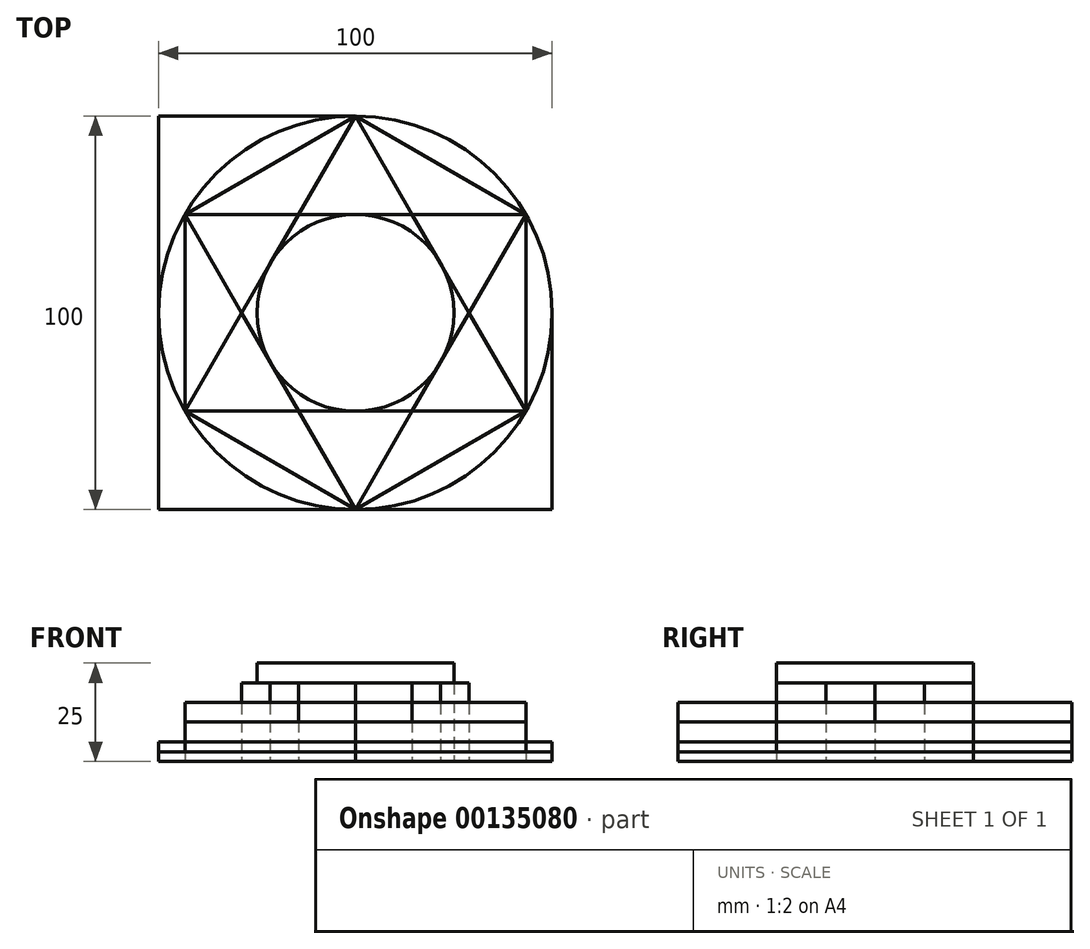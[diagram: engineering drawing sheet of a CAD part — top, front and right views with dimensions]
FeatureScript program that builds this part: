
annotation { "Feature Type Name" : "Feature", "Feature Type Description" : "" }
export const myFeature = defineFeature(function(context is Context, id is Id, definition is map)
    precondition{}
    {
        {
            var Q0;
            Q0=qCreatedBy(makeId("Top.planeOp"),FACE);
            var sketch = newSketch(context, id + "F0", { "sketchPlane" : qUnion([Q0])});
            skCircle(sketch, "E0", {"center": v(0, 0) * mm, "radius": 50 * mm});
            skCircle(sketch, "E1.cCircle", {"center": v(0, 0) * mm, "radius": 50 * mm, "construction": true});
            skLineSegment(sketch, "E1.0", {"start": v(0, 50) * mm, "end": v(43.3, 25) * mm});
            skLineSegment(sketch, "E1.1", {"start": v(43.3, 25) * mm, "end": v(43.3, -25) * mm});
            skLineSegment(sketch, "E1.2", {"start": v(43.3, -25) * mm, "end": v(0, -50) * mm});
            skLineSegment(sketch, "E1.3", {"start": v(0, -50) * mm, "end": v(-43.3, -25) * mm});
            skLineSegment(sketch, "E1.4", {"start": v(-43.3, -25) * mm, "end": v(-43.3, 25) * mm});
            skLineSegment(sketch, "E1.5", {"start": v(-43.3, 25) * mm, "end": v(0, 50) * mm});
            skLineSegment(sketch, "E2", {"start": v(0, 50) * mm, "end": v(-43.3, -25) * mm});
            skLineSegment(sketch, "E3", {"start": v(-43.3, -25) * mm, "end": v(43.3, -25) * mm});
            skLineSegment(sketch, "E4", {"start": v(43.3, -25) * mm, "end": v(0, 50) * mm});
            skLineSegment(sketch, "E5", {"start": v(-43.3, 25) * mm, "end": v(43.3, 25) * mm});
            skLineSegment(sketch, "E6", {"start": v(43.3, 25) * mm, "end": v(0, -50) * mm});
            skLineSegment(sketch, "E7", {"start": v(0, -50) * mm, "end": v(-43.3, 25) * mm});
            skCircle(sketch, "E8", {"center": v(0, 0) * mm, "radius": 25 * mm});
            skLineSegment(sketch, "E9", {"start": v(50, 50) * mm, "end": v(50, 0) * mm});
            skLineSegment(sketch, "E10.0", {"start": v(-50, 50) * mm, "end": v(50, 50) * mm});
            skLineSegment(sketch, "E10.1", {"start": v(50, 50) * mm, "end": v(50, -50) * mm});
            skLineSegment(sketch, "E10.2", {"start": v(50, -50) * mm, "end": v(-50, -50) * mm});
            skLineSegment(sketch, "E10.3", {"start": v(-50, -50) * mm, "end": v(-50, 50) * mm});
            skPoint(sketch, "E10.0.midPoint", {"position": v(0, 50) * mm});
            skSolve(sketch);
        }
        {
            var Q0;
            {var subQ0=sQuery(id+"F0.wireOp",EDGE,"E8");var subQ5=makeQuery(id+"F0.imprint","INTERSECT",VERTEX,{"derivedFrom":[sQuery(id+"F0.wireOp",EDGE,"E4"),subQ0]});Q0=makeQuery(id+"F0.imprint","IMPRINT",FACE,{"disambiguationData":[TD([[makeQuery(id+"F0.imprint","IMPRINT",EDGE,{"disambiguationData":[TD([[subQ5,-1.0]])],"derivedFrom":subQ0}),1.0]])]});}
            extrude(context, id + "F1", {"entities" : qUnion([Q0]), "depth" : 25 * mm});
        }
        {
            var Q0;
            {var subQ0=sQuery(id+"F0.wireOp",EDGE,"E5");var subQ1=sQuery(id+"F0.wireOp",EDGE,"E2");var subQ2=makeQuery(id+"F0.imprint","INTERSECT",VERTEX,{"derivedFrom":[subQ1,subQ0]});Q0=makeQuery(id+"F0.imprint","IMPRINT",FACE,{"disambiguationData":[TD([[makeQuery(id+"F0.imprint","IMPRINT",EDGE,{"disambiguationData":[TD([[subQ2,-1.0]])],"derivedFrom":subQ1}),1.0]])]});}
            var Q1;
            {var subQ0=sQuery(id+"F0.wireOp",EDGE,"E6");var subQ1=sQuery(id+"F0.wireOp",EDGE,"E4");var subQ2=makeQuery(id+"F0.imprint","INTERSECT",VERTEX,{"derivedFrom":[subQ1,subQ0]});Q1=makeQuery(id+"F0.imprint","IMPRINT",FACE,{"disambiguationData":[TD([[makeQuery(id+"F0.imprint","IMPRINT",EDGE,{"disambiguationData":[TD([[subQ2,-1.0]])],"derivedFrom":subQ1}),1.0]])]});}
            var Q2;
            {var subQ0=sQuery(id+"F0.wireOp",EDGE,"E8");var subQ1=sQuery(id+"F0.wireOp",EDGE,"E4");var subQ2=makeQuery(id+"F0.imprint","INTERSECT",VERTEX,{"derivedFrom":[subQ1,subQ0]});Q2=makeQuery(id+"F0.imprint","IMPRINT",FACE,{"disambiguationData":[TD([[makeQuery(id+"F0.imprint","IMPRINT",EDGE,{"disambiguationData":[TD([[subQ2,-1.0]])],"derivedFrom":subQ1}),1.0]])]});}
            var Q3;
            {var subQ0=sQuery(id+"F0.wireOp",EDGE,"E8");var subQ1=sQuery(id+"F0.wireOp",EDGE,"E3");var subQ2=makeQuery(id+"F0.imprint","INTERSECT",VERTEX,{"derivedFrom":[subQ1,subQ0]});Q3=makeQuery(id+"F0.imprint","IMPRINT",FACE,{"disambiguationData":[TD([[makeQuery(id+"F0.imprint","IMPRINT",EDGE,{"disambiguationData":[TD([[subQ2,-1.0]])],"derivedFrom":subQ1}),1.0]])]});}
            var Q4;
            {var subQ0=sQuery(id+"F0.wireOp",EDGE,"E7");var subQ1=sQuery(id+"F0.wireOp",EDGE,"E3");var subQ2=makeQuery(id+"F0.imprint","INTERSECT",VERTEX,{"derivedFrom":[subQ1,subQ0]});Q4=makeQuery(id+"F0.imprint","IMPRINT",FACE,{"disambiguationData":[TD([[makeQuery(id+"F0.imprint","IMPRINT",EDGE,{"disambiguationData":[TD([[subQ2,-1.0]])],"derivedFrom":subQ1}),1.0]])]});}
            var Q5;
            {var subQ0=sQuery(id+"F0.wireOp",EDGE,"E8");var subQ1=sQuery(id+"F0.wireOp",EDGE,"E2");var subQ2=makeQuery(id+"F0.imprint","INTERSECT",VERTEX,{"derivedFrom":[subQ1,subQ0]});Q5=makeQuery(id+"F0.imprint","IMPRINT",FACE,{"disambiguationData":[TD([[makeQuery(id+"F0.imprint","IMPRINT",EDGE,{"disambiguationData":[TD([[subQ2,-1.0]])],"derivedFrom":subQ1}),1.0]])]});}
            extrude(context, id + "F2", {"entities" : qUnion([Q0, Q1, Q2, Q3, Q4, Q5]), "depth" : 20 * mm});
        }
        {
            var Q0;
            {var subQ1=sQuery(id+"F0.wireOp",EDGE,"E2");var subQ3=sQuery(id+"F0.wireOp",EDGE,"E5");var subQ4=makeQuery(id+"F0.imprint","INTERSECT",VERTEX,{"derivedFrom":[subQ1,subQ3]});Q0=makeQuery(id+"F0.imprint","IMPRINT",FACE,{"disambiguationData":[TD([[makeQuery(id+"F0.imprint","IMPRINT",EDGE,{"disambiguationData":[TD([[subQ4,-1.0]])],"derivedFrom":subQ3}),1.0]])]});}
            var Q1;
            {var subQ0=sQuery(id+"F0.wireOp",EDGE,"E6");var subQ1=sQuery(id+"F0.wireOp",EDGE,"E4");var subQ2=makeQuery(id+"F0.imprint","INTERSECT",VERTEX,{"derivedFrom":[subQ1,subQ0]});Q1=makeQuery(id+"F0.imprint","IMPRINT",FACE,{"disambiguationData":[TD([[makeQuery(id+"F0.imprint","IMPRINT",EDGE,{"disambiguationData":[TD([[subQ2,-1.0]])],"derivedFrom":subQ1}),-1.0]])]});}
            var Q2;
            {var subQ0=sQuery(id+"F0.wireOp",EDGE,"E4");var subQ3=sQuery(id+"F0.wireOp",EDGE,"E6");var subQ5=makeQuery(id+"F0.imprint","INTERSECT",VERTEX,{"derivedFrom":[subQ0,subQ3]});Q2=makeQuery(id+"F0.imprint","IMPRINT",FACE,{"disambiguationData":[TD([[makeQuery(id+"F0.imprint","IMPRINT",EDGE,{"disambiguationData":[TD([[subQ5,-1.0]])],"derivedFrom":subQ3}),1.0]])]});}
            var Q3;
            {var subQ0=sQuery(id+"F0.wireOp",EDGE,"E7");var subQ1=sQuery(id+"F0.wireOp",EDGE,"E3");var subQ2=makeQuery(id+"F0.imprint","INTERSECT",VERTEX,{"derivedFrom":[subQ1,subQ0]});Q3=makeQuery(id+"F0.imprint","IMPRINT",FACE,{"disambiguationData":[TD([[makeQuery(id+"F0.imprint","IMPRINT",EDGE,{"disambiguationData":[TD([[subQ2,-1.0]])],"derivedFrom":subQ1}),-1.0]])]});}
            var Q4;
            {var subQ0=sQuery(id+"F0.wireOp",EDGE,"E3");var subQ3=sQuery(id+"F0.wireOp",EDGE,"E7");var subQ5=makeQuery(id+"F0.imprint","INTERSECT",VERTEX,{"derivedFrom":[subQ0,subQ3]});Q4=makeQuery(id+"F0.imprint","IMPRINT",FACE,{"disambiguationData":[TD([[makeQuery(id+"F0.imprint","IMPRINT",EDGE,{"disambiguationData":[TD([[subQ5,-1.0]])],"derivedFrom":subQ3}),1.0]])]});}
            var Q5;
            {var subQ0=sQuery(id+"F0.wireOp",EDGE,"E5");var subQ1=sQuery(id+"F0.wireOp",EDGE,"E2");var subQ2=makeQuery(id+"F0.imprint","INTERSECT",VERTEX,{"derivedFrom":[subQ1,subQ0]});Q5=makeQuery(id+"F0.imprint","IMPRINT",FACE,{"disambiguationData":[TD([[makeQuery(id+"F0.imprint","IMPRINT",EDGE,{"disambiguationData":[TD([[subQ2,-1.0]])],"derivedFrom":subQ1}),-1.0]])]});}
            var Q6;
            {var subQ0=sQuery(id+"F0.wireOp",EDGE,"E5");var subQ1=sQuery(id+"F0.wireOp",EDGE,"E2");var subQ2=makeQuery(id+"F0.imprint","INTERSECT",VERTEX,{"derivedFrom":[subQ1,subQ0]});Q6=makeQuery(id+"F0.imprint","IMPRINT",FACE,{"disambiguationData":[TD([[makeQuery(id+"F0.imprint","IMPRINT",EDGE,{"disambiguationData":[TD([[subQ2,-1.0]])],"derivedFrom":subQ1}),1.0]])]});}
            var Q7;
            {var subQ0=sQuery(id+"F0.wireOp",EDGE,"E8");var subQ1=sQuery(id+"F0.wireOp",EDGE,"E4");var subQ2=makeQuery(id+"F0.imprint","INTERSECT",VERTEX,{"derivedFrom":[subQ1,subQ0]});Q7=makeQuery(id+"F0.imprint","IMPRINT",FACE,{"disambiguationData":[TD([[makeQuery(id+"F0.imprint","IMPRINT",EDGE,{"disambiguationData":[TD([[subQ2,-1.0]])],"derivedFrom":subQ1}),1.0]])]});}
            var Q8;
            {var subQ0=sQuery(id+"F0.wireOp",EDGE,"E6");var subQ1=sQuery(id+"F0.wireOp",EDGE,"E4");var subQ2=makeQuery(id+"F0.imprint","INTERSECT",VERTEX,{"derivedFrom":[subQ1,subQ0]});Q8=makeQuery(id+"F0.imprint","IMPRINT",FACE,{"disambiguationData":[TD([[makeQuery(id+"F0.imprint","IMPRINT",EDGE,{"disambiguationData":[TD([[subQ2,-1.0]])],"derivedFrom":subQ1}),1.0]])]});}
            var Q9;
            {var subQ0=sQuery(id+"F0.wireOp",EDGE,"E8");var subQ1=sQuery(id+"F0.wireOp",EDGE,"E3");var subQ2=makeQuery(id+"F0.imprint","INTERSECT",VERTEX,{"derivedFrom":[subQ1,subQ0]});Q9=makeQuery(id+"F0.imprint","IMPRINT",FACE,{"disambiguationData":[TD([[makeQuery(id+"F0.imprint","IMPRINT",EDGE,{"disambiguationData":[TD([[subQ2,-1.0]])],"derivedFrom":subQ1}),1.0]])]});}
            var Q10;
            {var subQ0=sQuery(id+"F0.wireOp",EDGE,"E7");var subQ1=sQuery(id+"F0.wireOp",EDGE,"E3");var subQ2=makeQuery(id+"F0.imprint","INTERSECT",VERTEX,{"derivedFrom":[subQ1,subQ0]});Q10=makeQuery(id+"F0.imprint","IMPRINT",FACE,{"disambiguationData":[TD([[makeQuery(id+"F0.imprint","IMPRINT",EDGE,{"disambiguationData":[TD([[subQ2,-1.0]])],"derivedFrom":subQ1}),1.0]])]});}
            var Q11;
            {var subQ0=sQuery(id+"F0.wireOp",EDGE,"E8");var subQ1=sQuery(id+"F0.wireOp",EDGE,"E2");var subQ2=makeQuery(id+"F0.imprint","INTERSECT",VERTEX,{"derivedFrom":[subQ1,subQ0]});Q11=makeQuery(id+"F0.imprint","IMPRINT",FACE,{"disambiguationData":[TD([[makeQuery(id+"F0.imprint","IMPRINT",EDGE,{"disambiguationData":[TD([[subQ2,-1.0]])],"derivedFrom":subQ1}),1.0]])]});}
            var Q12;
            {var subQ0=sQuery(id+"F0.wireOp",EDGE,"E8");var subQ5=makeQuery(id+"F0.imprint","INTERSECT",VERTEX,{"derivedFrom":[sQuery(id+"F0.wireOp",EDGE,"E4"),subQ0]});Q12=makeQuery(id+"F0.imprint","IMPRINT",FACE,{"disambiguationData":[TD([[makeQuery(id+"F0.imprint","IMPRINT",EDGE,{"disambiguationData":[TD([[subQ5,-1.0]])],"derivedFrom":subQ0}),1.0]])]});}
            extrude(context, id + "F3", {"entities" : qUnion([Q0, Q1, Q2, Q3, Q4, Q5, Q6, Q7, Q8, Q9, Q10, Q11, Q12]), "depth" : 15 * mm});
        }
        {
            var Q0;
            {var subQ0=sQuery(id+"F0.wireOp",EDGE,"E1.5");Q0=makeQuery(id+"F0.imprint","IMPRINT",FACE,{"disambiguationData":[TD([[makeQuery(id+"F0.imprint","IMPRINT",EDGE,{"derivedFrom":subQ0}),-1.0]])]});}
            var Q1;
            {var subQ0=sQuery(id+"F0.wireOp",EDGE,"E1.0");Q1=makeQuery(id+"F0.imprint","IMPRINT",FACE,{"disambiguationData":[TD([[makeQuery(id+"F0.imprint","IMPRINT",EDGE,{"derivedFrom":subQ0}),-1.0]])]});}
            var Q2;
            {var subQ0=sQuery(id+"F0.wireOp",EDGE,"E1.1");Q2=makeQuery(id+"F0.imprint","IMPRINT",FACE,{"disambiguationData":[TD([[makeQuery(id+"F0.imprint","IMPRINT",EDGE,{"derivedFrom":subQ0}),-1.0]])]});}
            var Q3;
            {var subQ0=sQuery(id+"F0.wireOp",EDGE,"E1.2");Q3=makeQuery(id+"F0.imprint","IMPRINT",FACE,{"disambiguationData":[TD([[makeQuery(id+"F0.imprint","IMPRINT",EDGE,{"derivedFrom":subQ0}),-1.0]])]});}
            var Q4;
            {var subQ0=sQuery(id+"F0.wireOp",EDGE,"E1.3");Q4=makeQuery(id+"F0.imprint","IMPRINT",FACE,{"disambiguationData":[TD([[makeQuery(id+"F0.imprint","IMPRINT",EDGE,{"derivedFrom":subQ0}),-1.0]])]});}
            var Q5;
            {var subQ0=sQuery(id+"F0.wireOp",EDGE,"E1.4");Q5=makeQuery(id+"F0.imprint","IMPRINT",FACE,{"disambiguationData":[TD([[makeQuery(id+"F0.imprint","IMPRINT",EDGE,{"derivedFrom":subQ0}),-1.0]])]});}
            var Q6;
            {var subQ0=sQuery(id+"F0.wireOp",EDGE,"E5");var subQ1=sQuery(id+"F0.wireOp",EDGE,"E2");var subQ2=makeQuery(id+"F0.imprint","INTERSECT",VERTEX,{"derivedFrom":[subQ1,subQ0]});Q6=makeQuery(id+"F0.imprint","IMPRINT",FACE,{"disambiguationData":[TD([[makeQuery(id+"F0.imprint","IMPRINT",EDGE,{"disambiguationData":[TD([[subQ2,-1.0]])],"derivedFrom":subQ1}),-1.0]])]});}
            var Q7;
            {var subQ1=sQuery(id+"F0.wireOp",EDGE,"E2");var subQ3=sQuery(id+"F0.wireOp",EDGE,"E5");var subQ4=makeQuery(id+"F0.imprint","INTERSECT",VERTEX,{"derivedFrom":[subQ1,subQ3]});Q7=makeQuery(id+"F0.imprint","IMPRINT",FACE,{"disambiguationData":[TD([[makeQuery(id+"F0.imprint","IMPRINT",EDGE,{"disambiguationData":[TD([[subQ4,-1.0]])],"derivedFrom":subQ3}),1.0]])]});}
            var Q8;
            {var subQ0=sQuery(id+"F0.wireOp",EDGE,"E6");var subQ1=sQuery(id+"F0.wireOp",EDGE,"E4");var subQ2=makeQuery(id+"F0.imprint","INTERSECT",VERTEX,{"derivedFrom":[subQ1,subQ0]});Q8=makeQuery(id+"F0.imprint","IMPRINT",FACE,{"disambiguationData":[TD([[makeQuery(id+"F0.imprint","IMPRINT",EDGE,{"disambiguationData":[TD([[subQ2,-1.0]])],"derivedFrom":subQ1}),-1.0]])]});}
            var Q9;
            {var subQ0=sQuery(id+"F0.wireOp",EDGE,"E4");var subQ3=sQuery(id+"F0.wireOp",EDGE,"E6");var subQ5=makeQuery(id+"F0.imprint","INTERSECT",VERTEX,{"derivedFrom":[subQ0,subQ3]});Q9=makeQuery(id+"F0.imprint","IMPRINT",FACE,{"disambiguationData":[TD([[makeQuery(id+"F0.imprint","IMPRINT",EDGE,{"disambiguationData":[TD([[subQ5,-1.0]])],"derivedFrom":subQ3}),1.0]])]});}
            var Q10;
            {var subQ0=sQuery(id+"F0.wireOp",EDGE,"E7");var subQ1=sQuery(id+"F0.wireOp",EDGE,"E3");var subQ2=makeQuery(id+"F0.imprint","INTERSECT",VERTEX,{"derivedFrom":[subQ1,subQ0]});Q10=makeQuery(id+"F0.imprint","IMPRINT",FACE,{"disambiguationData":[TD([[makeQuery(id+"F0.imprint","IMPRINT",EDGE,{"disambiguationData":[TD([[subQ2,-1.0]])],"derivedFrom":subQ1}),-1.0]])]});}
            var Q11;
            {var subQ0=sQuery(id+"F0.wireOp",EDGE,"E3");var subQ3=sQuery(id+"F0.wireOp",EDGE,"E7");var subQ5=makeQuery(id+"F0.imprint","INTERSECT",VERTEX,{"derivedFrom":[subQ0,subQ3]});Q11=makeQuery(id+"F0.imprint","IMPRINT",FACE,{"disambiguationData":[TD([[makeQuery(id+"F0.imprint","IMPRINT",EDGE,{"disambiguationData":[TD([[subQ5,-1.0]])],"derivedFrom":subQ3}),1.0]])]});}
            var Q12;
            {var subQ0=sQuery(id+"F0.wireOp",EDGE,"E8");var subQ1=sQuery(id+"F0.wireOp",EDGE,"E2");var subQ2=makeQuery(id+"F0.imprint","INTERSECT",VERTEX,{"derivedFrom":[subQ1,subQ0]});Q12=makeQuery(id+"F0.imprint","IMPRINT",FACE,{"disambiguationData":[TD([[makeQuery(id+"F0.imprint","IMPRINT",EDGE,{"disambiguationData":[TD([[subQ2,-1.0]])],"derivedFrom":subQ1}),1.0]])]});}
            var Q13;
            {var subQ0=sQuery(id+"F0.wireOp",EDGE,"E5");var subQ1=sQuery(id+"F0.wireOp",EDGE,"E2");var subQ2=makeQuery(id+"F0.imprint","INTERSECT",VERTEX,{"derivedFrom":[subQ1,subQ0]});Q13=makeQuery(id+"F0.imprint","IMPRINT",FACE,{"disambiguationData":[TD([[makeQuery(id+"F0.imprint","IMPRINT",EDGE,{"disambiguationData":[TD([[subQ2,-1.0]])],"derivedFrom":subQ1}),1.0]])]});}
            var Q14;
            {var subQ0=sQuery(id+"F0.wireOp",EDGE,"E8");var subQ1=sQuery(id+"F0.wireOp",EDGE,"E4");var subQ2=makeQuery(id+"F0.imprint","INTERSECT",VERTEX,{"derivedFrom":[subQ1,subQ0]});Q14=makeQuery(id+"F0.imprint","IMPRINT",FACE,{"disambiguationData":[TD([[makeQuery(id+"F0.imprint","IMPRINT",EDGE,{"disambiguationData":[TD([[subQ2,-1.0]])],"derivedFrom":subQ1}),1.0]])]});}
            var Q15;
            {var subQ0=sQuery(id+"F0.wireOp",EDGE,"E6");var subQ1=sQuery(id+"F0.wireOp",EDGE,"E4");var subQ2=makeQuery(id+"F0.imprint","INTERSECT",VERTEX,{"derivedFrom":[subQ1,subQ0]});Q15=makeQuery(id+"F0.imprint","IMPRINT",FACE,{"disambiguationData":[TD([[makeQuery(id+"F0.imprint","IMPRINT",EDGE,{"disambiguationData":[TD([[subQ2,-1.0]])],"derivedFrom":subQ1}),1.0]])]});}
            var Q16;
            {var subQ0=sQuery(id+"F0.wireOp",EDGE,"E8");var subQ1=sQuery(id+"F0.wireOp",EDGE,"E3");var subQ2=makeQuery(id+"F0.imprint","INTERSECT",VERTEX,{"derivedFrom":[subQ1,subQ0]});Q16=makeQuery(id+"F0.imprint","IMPRINT",FACE,{"disambiguationData":[TD([[makeQuery(id+"F0.imprint","IMPRINT",EDGE,{"disambiguationData":[TD([[subQ2,-1.0]])],"derivedFrom":subQ1}),1.0]])]});}
            var Q17;
            {var subQ0=sQuery(id+"F0.wireOp",EDGE,"E7");var subQ1=sQuery(id+"F0.wireOp",EDGE,"E3");var subQ2=makeQuery(id+"F0.imprint","INTERSECT",VERTEX,{"derivedFrom":[subQ1,subQ0]});Q17=makeQuery(id+"F0.imprint","IMPRINT",FACE,{"disambiguationData":[TD([[makeQuery(id+"F0.imprint","IMPRINT",EDGE,{"disambiguationData":[TD([[subQ2,-1.0]])],"derivedFrom":subQ1}),1.0]])]});}
            var Q18;
            {var subQ0=sQuery(id+"F0.wireOp",EDGE,"E8");var subQ5=makeQuery(id+"F0.imprint","INTERSECT",VERTEX,{"derivedFrom":[sQuery(id+"F0.wireOp",EDGE,"E4"),subQ0]});Q18=makeQuery(id+"F0.imprint","IMPRINT",FACE,{"disambiguationData":[TD([[makeQuery(id+"F0.imprint","IMPRINT",EDGE,{"disambiguationData":[TD([[subQ5,-1.0]])],"derivedFrom":subQ0}),1.0]])]});}
            extrude(context, id + "F4", {"entities" : qUnion([Q0, Q1, Q2, Q3, Q4, Q5, Q6, Q7, Q8, Q9, Q10, Q11, Q12, Q13, Q14, Q15, Q16, Q17, Q18]), "depth" : 10 * mm});
        }
        {
            var Q0;
            {var subQ0=sQuery(id+"F0.wireOp",EDGE,"E1.5");Q0=makeQuery(id+"F0.imprint","IMPRINT",FACE,{"disambiguationData":[TD([[makeQuery(id+"F0.imprint","IMPRINT",EDGE,{"derivedFrom":subQ0}),1.0]])]});}
            var Q1;
            {var subQ0=sQuery(id+"F0.wireOp",EDGE,"E1.0");Q1=makeQuery(id+"F0.imprint","IMPRINT",FACE,{"disambiguationData":[TD([[makeQuery(id+"F0.imprint","IMPRINT",EDGE,{"derivedFrom":subQ0}),1.0]])]});}
            var Q2;
            {var subQ0=sQuery(id+"F0.wireOp",EDGE,"E1.1");Q2=makeQuery(id+"F0.imprint","IMPRINT",FACE,{"disambiguationData":[TD([[makeQuery(id+"F0.imprint","IMPRINT",EDGE,{"derivedFrom":subQ0}),1.0]])]});}
            var Q3;
            {var subQ0=sQuery(id+"F0.wireOp",EDGE,"E1.2");Q3=makeQuery(id+"F0.imprint","IMPRINT",FACE,{"disambiguationData":[TD([[makeQuery(id+"F0.imprint","IMPRINT",EDGE,{"derivedFrom":subQ0}),1.0]])]});}
            var Q4;
            {var subQ0=sQuery(id+"F0.wireOp",EDGE,"E1.3");Q4=makeQuery(id+"F0.imprint","IMPRINT",FACE,{"disambiguationData":[TD([[makeQuery(id+"F0.imprint","IMPRINT",EDGE,{"derivedFrom":subQ0}),1.0]])]});}
            var Q5;
            {var subQ0=sQuery(id+"F0.wireOp",EDGE,"E1.4");Q5=makeQuery(id+"F0.imprint","IMPRINT",FACE,{"disambiguationData":[TD([[makeQuery(id+"F0.imprint","IMPRINT",EDGE,{"derivedFrom":subQ0}),1.0]])]});}
            var Q6;
            {var subQ0=sQuery(id+"F0.wireOp",EDGE,"E1.5");Q6=makeQuery(id+"F0.imprint","IMPRINT",FACE,{"disambiguationData":[TD([[makeQuery(id+"F0.imprint","IMPRINT",EDGE,{"derivedFrom":subQ0}),-1.0]])]});}
            var Q7;
            {var subQ0=sQuery(id+"F0.wireOp",EDGE,"E1.0");Q7=makeQuery(id+"F0.imprint","IMPRINT",FACE,{"disambiguationData":[TD([[makeQuery(id+"F0.imprint","IMPRINT",EDGE,{"derivedFrom":subQ0}),-1.0]])]});}
            var Q8;
            {var subQ0=sQuery(id+"F0.wireOp",EDGE,"E1.1");Q8=makeQuery(id+"F0.imprint","IMPRINT",FACE,{"disambiguationData":[TD([[makeQuery(id+"F0.imprint","IMPRINT",EDGE,{"derivedFrom":subQ0}),-1.0]])]});}
            var Q9;
            {var subQ0=sQuery(id+"F0.wireOp",EDGE,"E1.2");Q9=makeQuery(id+"F0.imprint","IMPRINT",FACE,{"disambiguationData":[TD([[makeQuery(id+"F0.imprint","IMPRINT",EDGE,{"derivedFrom":subQ0}),-1.0]])]});}
            var Q10;
            {var subQ0=sQuery(id+"F0.wireOp",EDGE,"E1.3");Q10=makeQuery(id+"F0.imprint","IMPRINT",FACE,{"disambiguationData":[TD([[makeQuery(id+"F0.imprint","IMPRINT",EDGE,{"derivedFrom":subQ0}),-1.0]])]});}
            var Q11;
            {var subQ0=sQuery(id+"F0.wireOp",EDGE,"E1.4");Q11=makeQuery(id+"F0.imprint","IMPRINT",FACE,{"disambiguationData":[TD([[makeQuery(id+"F0.imprint","IMPRINT",EDGE,{"derivedFrom":subQ0}),-1.0]])]});}
            var Q12;
            {var subQ1=sQuery(id+"F0.wireOp",EDGE,"E2");var subQ3=sQuery(id+"F0.wireOp",EDGE,"E5");var subQ4=makeQuery(id+"F0.imprint","INTERSECT",VERTEX,{"derivedFrom":[subQ1,subQ3]});Q12=makeQuery(id+"F0.imprint","IMPRINT",FACE,{"disambiguationData":[TD([[makeQuery(id+"F0.imprint","IMPRINT",EDGE,{"disambiguationData":[TD([[subQ4,-1.0]])],"derivedFrom":subQ3}),1.0]])]});}
            var Q13;
            {var subQ0=sQuery(id+"F0.wireOp",EDGE,"E6");var subQ1=sQuery(id+"F0.wireOp",EDGE,"E4");var subQ2=makeQuery(id+"F0.imprint","INTERSECT",VERTEX,{"derivedFrom":[subQ1,subQ0]});Q13=makeQuery(id+"F0.imprint","IMPRINT",FACE,{"disambiguationData":[TD([[makeQuery(id+"F0.imprint","IMPRINT",EDGE,{"disambiguationData":[TD([[subQ2,-1.0]])],"derivedFrom":subQ1}),-1.0]])]});}
            var Q14;
            {var subQ0=sQuery(id+"F0.wireOp",EDGE,"E4");var subQ3=sQuery(id+"F0.wireOp",EDGE,"E6");var subQ5=makeQuery(id+"F0.imprint","INTERSECT",VERTEX,{"derivedFrom":[subQ0,subQ3]});Q14=makeQuery(id+"F0.imprint","IMPRINT",FACE,{"disambiguationData":[TD([[makeQuery(id+"F0.imprint","IMPRINT",EDGE,{"disambiguationData":[TD([[subQ5,-1.0]])],"derivedFrom":subQ3}),1.0]])]});}
            var Q15;
            {var subQ0=sQuery(id+"F0.wireOp",EDGE,"E7");var subQ1=sQuery(id+"F0.wireOp",EDGE,"E3");var subQ2=makeQuery(id+"F0.imprint","INTERSECT",VERTEX,{"derivedFrom":[subQ1,subQ0]});Q15=makeQuery(id+"F0.imprint","IMPRINT",FACE,{"disambiguationData":[TD([[makeQuery(id+"F0.imprint","IMPRINT",EDGE,{"disambiguationData":[TD([[subQ2,-1.0]])],"derivedFrom":subQ1}),-1.0]])]});}
            var Q16;
            {var subQ0=sQuery(id+"F0.wireOp",EDGE,"E3");var subQ3=sQuery(id+"F0.wireOp",EDGE,"E7");var subQ5=makeQuery(id+"F0.imprint","INTERSECT",VERTEX,{"derivedFrom":[subQ0,subQ3]});Q16=makeQuery(id+"F0.imprint","IMPRINT",FACE,{"disambiguationData":[TD([[makeQuery(id+"F0.imprint","IMPRINT",EDGE,{"disambiguationData":[TD([[subQ5,-1.0]])],"derivedFrom":subQ3}),1.0]])]});}
            var Q17;
            {var subQ0=sQuery(id+"F0.wireOp",EDGE,"E5");var subQ1=sQuery(id+"F0.wireOp",EDGE,"E2");var subQ2=makeQuery(id+"F0.imprint","INTERSECT",VERTEX,{"derivedFrom":[subQ1,subQ0]});Q17=makeQuery(id+"F0.imprint","IMPRINT",FACE,{"disambiguationData":[TD([[makeQuery(id+"F0.imprint","IMPRINT",EDGE,{"disambiguationData":[TD([[subQ2,-1.0]])],"derivedFrom":subQ1}),-1.0]])]});}
            var Q18;
            {var subQ0=sQuery(id+"F0.wireOp",EDGE,"E5");var subQ1=sQuery(id+"F0.wireOp",EDGE,"E2");var subQ2=makeQuery(id+"F0.imprint","INTERSECT",VERTEX,{"derivedFrom":[subQ1,subQ0]});Q18=makeQuery(id+"F0.imprint","IMPRINT",FACE,{"disambiguationData":[TD([[makeQuery(id+"F0.imprint","IMPRINT",EDGE,{"disambiguationData":[TD([[subQ2,-1.0]])],"derivedFrom":subQ1}),1.0]])]});}
            var Q19;
            {var subQ0=sQuery(id+"F0.wireOp",EDGE,"E8");var subQ1=sQuery(id+"F0.wireOp",EDGE,"E4");var subQ2=makeQuery(id+"F0.imprint","INTERSECT",VERTEX,{"derivedFrom":[subQ1,subQ0]});Q19=makeQuery(id+"F0.imprint","IMPRINT",FACE,{"disambiguationData":[TD([[makeQuery(id+"F0.imprint","IMPRINT",EDGE,{"disambiguationData":[TD([[subQ2,-1.0]])],"derivedFrom":subQ1}),1.0]])]});}
            var Q20;
            {var subQ0=sQuery(id+"F0.wireOp",EDGE,"E6");var subQ1=sQuery(id+"F0.wireOp",EDGE,"E4");var subQ2=makeQuery(id+"F0.imprint","INTERSECT",VERTEX,{"derivedFrom":[subQ1,subQ0]});Q20=makeQuery(id+"F0.imprint","IMPRINT",FACE,{"disambiguationData":[TD([[makeQuery(id+"F0.imprint","IMPRINT",EDGE,{"disambiguationData":[TD([[subQ2,-1.0]])],"derivedFrom":subQ1}),1.0]])]});}
            var Q21;
            {var subQ0=sQuery(id+"F0.wireOp",EDGE,"E8");var subQ1=sQuery(id+"F0.wireOp",EDGE,"E3");var subQ2=makeQuery(id+"F0.imprint","INTERSECT",VERTEX,{"derivedFrom":[subQ1,subQ0]});Q21=makeQuery(id+"F0.imprint","IMPRINT",FACE,{"disambiguationData":[TD([[makeQuery(id+"F0.imprint","IMPRINT",EDGE,{"disambiguationData":[TD([[subQ2,-1.0]])],"derivedFrom":subQ1}),1.0]])]});}
            var Q22;
            {var subQ0=sQuery(id+"F0.wireOp",EDGE,"E7");var subQ1=sQuery(id+"F0.wireOp",EDGE,"E3");var subQ2=makeQuery(id+"F0.imprint","INTERSECT",VERTEX,{"derivedFrom":[subQ1,subQ0]});Q22=makeQuery(id+"F0.imprint","IMPRINT",FACE,{"disambiguationData":[TD([[makeQuery(id+"F0.imprint","IMPRINT",EDGE,{"disambiguationData":[TD([[subQ2,-1.0]])],"derivedFrom":subQ1}),1.0]])]});}
            var Q23;
            {var subQ0=sQuery(id+"F0.wireOp",EDGE,"E8");var subQ1=sQuery(id+"F0.wireOp",EDGE,"E2");var subQ2=makeQuery(id+"F0.imprint","INTERSECT",VERTEX,{"derivedFrom":[subQ1,subQ0]});Q23=makeQuery(id+"F0.imprint","IMPRINT",FACE,{"disambiguationData":[TD([[makeQuery(id+"F0.imprint","IMPRINT",EDGE,{"disambiguationData":[TD([[subQ2,-1.0]])],"derivedFrom":subQ1}),1.0]])]});}
            var Q24;
            {var subQ0=sQuery(id+"F0.wireOp",EDGE,"E8");var subQ5=makeQuery(id+"F0.imprint","INTERSECT",VERTEX,{"derivedFrom":[sQuery(id+"F0.wireOp",EDGE,"E4"),subQ0]});Q24=makeQuery(id+"F0.imprint","IMPRINT",FACE,{"disambiguationData":[TD([[makeQuery(id+"F0.imprint","IMPRINT",EDGE,{"disambiguationData":[TD([[subQ5,-1.0]])],"derivedFrom":subQ0}),1.0]])]});}
            extrude(context, id + "F5", {"entities" : qUnion([Q0, Q1, Q2, Q3, Q4, Q5, Q6, Q7, Q8, Q9, Q10, Q11, Q12, Q13, Q14, Q15, Q16, Q17, Q18, Q19, Q20, Q21, Q22, Q23, Q24]), "depth" : 5 * mm});
        }
        {
            var Q0;
            {var subQ0=sQuery(id+"F0.wireOp",EDGE,"E10.0");var subQ5=sQuery(id+"F0.wireOp",EDGE,"E10.3");var subQ7=makeQuery(id+"F0.imprint","INTERSECT",VERTEX,{"derivedFrom":[subQ0,subQ5]});Q0=makeQuery(id+"F0.imprint","IMPRINT",FACE,{"disambiguationData":[TD([[makeQuery(id+"F0.imprint","IMPRINT",EDGE,{"disambiguationData":[TD([[subQ7,1.0]])],"derivedFrom":subQ5}),-1.0]])]});}
            var Q1;
            {var subQ3=sQuery(id+"F0.wireOp",EDGE,"E10.1");var subQ5=sQuery(id+"F0.wireOp",EDGE,"E10.0");var subQ7=makeQuery(id+"F0.imprint","INTERSECT",VERTEX,{"derivedFrom":[subQ5,subQ3]});Q1=makeQuery(id+"F0.imprint","IMPRINT",FACE,{"disambiguationData":[TD([[makeQuery(id+"F0.imprint","IMPRINT",EDGE,{"disambiguationData":[TD([[subQ7,-1.0]])],"derivedFrom":subQ3}),-1.0]])]});}
            var Q2;
            {var subQ3=sQuery(id+"F0.wireOp",EDGE,"E10.2");var subQ5=sQuery(id+"F0.wireOp",EDGE,"E10.1");var subQ7=makeQuery(id+"F0.imprint","INTERSECT",VERTEX,{"derivedFrom":[subQ5,subQ3]});Q2=makeQuery(id+"F0.imprint","IMPRINT",FACE,{"disambiguationData":[TD([[makeQuery(id+"F0.imprint","IMPRINT",EDGE,{"disambiguationData":[TD([[subQ7,1.0]])],"derivedFrom":subQ5}),-1.0]])]});}
            var Q3;
            {var subQ3=sQuery(id+"F0.wireOp",EDGE,"E10.3");var subQ5=sQuery(id+"F0.wireOp",EDGE,"E10.2");var subQ7=makeQuery(id+"F0.imprint","INTERSECT",VERTEX,{"derivedFrom":[subQ5,subQ3]});Q3=makeQuery(id+"F0.imprint","IMPRINT",FACE,{"disambiguationData":[TD([[makeQuery(id+"F0.imprint","IMPRINT",EDGE,{"disambiguationData":[TD([[subQ7,-1.0]])],"derivedFrom":subQ3}),-1.0]])]});}
            var Q4;
            {var subQ0=sQuery(id+"F0.wireOp",EDGE,"E1.5");Q4=makeQuery(id+"F0.imprint","IMPRINT",FACE,{"disambiguationData":[TD([[makeQuery(id+"F0.imprint","IMPRINT",EDGE,{"derivedFrom":subQ0}),1.0]])]});}
            var Q5;
            {var subQ0=sQuery(id+"F0.wireOp",EDGE,"E1.0");Q5=makeQuery(id+"F0.imprint","IMPRINT",FACE,{"disambiguationData":[TD([[makeQuery(id+"F0.imprint","IMPRINT",EDGE,{"derivedFrom":subQ0}),1.0]])]});}
            var Q6;
            {var subQ0=sQuery(id+"F0.wireOp",EDGE,"E1.1");Q6=makeQuery(id+"F0.imprint","IMPRINT",FACE,{"disambiguationData":[TD([[makeQuery(id+"F0.imprint","IMPRINT",EDGE,{"derivedFrom":subQ0}),1.0]])]});}
            var Q7;
            {var subQ0=sQuery(id+"F0.wireOp",EDGE,"E1.2");Q7=makeQuery(id+"F0.imprint","IMPRINT",FACE,{"disambiguationData":[TD([[makeQuery(id+"F0.imprint","IMPRINT",EDGE,{"derivedFrom":subQ0}),1.0]])]});}
            var Q8;
            {var subQ0=sQuery(id+"F0.wireOp",EDGE,"E1.3");Q8=makeQuery(id+"F0.imprint","IMPRINT",FACE,{"disambiguationData":[TD([[makeQuery(id+"F0.imprint","IMPRINT",EDGE,{"derivedFrom":subQ0}),1.0]])]});}
            var Q9;
            {var subQ0=sQuery(id+"F0.wireOp",EDGE,"E1.4");Q9=makeQuery(id+"F0.imprint","IMPRINT",FACE,{"disambiguationData":[TD([[makeQuery(id+"F0.imprint","IMPRINT",EDGE,{"derivedFrom":subQ0}),1.0]])]});}
            var Q10;
            {var subQ0=sQuery(id+"F0.wireOp",EDGE,"E1.5");Q10=makeQuery(id+"F0.imprint","IMPRINT",FACE,{"disambiguationData":[TD([[makeQuery(id+"F0.imprint","IMPRINT",EDGE,{"derivedFrom":subQ0}),-1.0]])]});}
            var Q11;
            {var subQ0=sQuery(id+"F0.wireOp",EDGE,"E1.0");Q11=makeQuery(id+"F0.imprint","IMPRINT",FACE,{"disambiguationData":[TD([[makeQuery(id+"F0.imprint","IMPRINT",EDGE,{"derivedFrom":subQ0}),-1.0]])]});}
            var Q12;
            {var subQ0=sQuery(id+"F0.wireOp",EDGE,"E1.1");Q12=makeQuery(id+"F0.imprint","IMPRINT",FACE,{"disambiguationData":[TD([[makeQuery(id+"F0.imprint","IMPRINT",EDGE,{"derivedFrom":subQ0}),-1.0]])]});}
            var Q13;
            {var subQ0=sQuery(id+"F0.wireOp",EDGE,"E1.2");Q13=makeQuery(id+"F0.imprint","IMPRINT",FACE,{"disambiguationData":[TD([[makeQuery(id+"F0.imprint","IMPRINT",EDGE,{"derivedFrom":subQ0}),-1.0]])]});}
            var Q14;
            {var subQ0=sQuery(id+"F0.wireOp",EDGE,"E1.3");Q14=makeQuery(id+"F0.imprint","IMPRINT",FACE,{"disambiguationData":[TD([[makeQuery(id+"F0.imprint","IMPRINT",EDGE,{"derivedFrom":subQ0}),-1.0]])]});}
            var Q15;
            {var subQ0=sQuery(id+"F0.wireOp",EDGE,"E1.4");Q15=makeQuery(id+"F0.imprint","IMPRINT",FACE,{"disambiguationData":[TD([[makeQuery(id+"F0.imprint","IMPRINT",EDGE,{"derivedFrom":subQ0}),-1.0]])]});}
            var Q16;
            {var subQ1=sQuery(id+"F0.wireOp",EDGE,"E2");var subQ3=sQuery(id+"F0.wireOp",EDGE,"E5");var subQ4=makeQuery(id+"F0.imprint","INTERSECT",VERTEX,{"derivedFrom":[subQ1,subQ3]});Q16=makeQuery(id+"F0.imprint","IMPRINT",FACE,{"disambiguationData":[TD([[makeQuery(id+"F0.imprint","IMPRINT",EDGE,{"disambiguationData":[TD([[subQ4,-1.0]])],"derivedFrom":subQ3}),1.0]])]});}
            var Q17;
            {var subQ0=sQuery(id+"F0.wireOp",EDGE,"E6");var subQ1=sQuery(id+"F0.wireOp",EDGE,"E4");var subQ2=makeQuery(id+"F0.imprint","INTERSECT",VERTEX,{"derivedFrom":[subQ1,subQ0]});Q17=makeQuery(id+"F0.imprint","IMPRINT",FACE,{"disambiguationData":[TD([[makeQuery(id+"F0.imprint","IMPRINT",EDGE,{"disambiguationData":[TD([[subQ2,-1.0]])],"derivedFrom":subQ1}),-1.0]])]});}
            var Q18;
            {var subQ0=sQuery(id+"F0.wireOp",EDGE,"E4");var subQ3=sQuery(id+"F0.wireOp",EDGE,"E6");var subQ5=makeQuery(id+"F0.imprint","INTERSECT",VERTEX,{"derivedFrom":[subQ0,subQ3]});Q18=makeQuery(id+"F0.imprint","IMPRINT",FACE,{"disambiguationData":[TD([[makeQuery(id+"F0.imprint","IMPRINT",EDGE,{"disambiguationData":[TD([[subQ5,-1.0]])],"derivedFrom":subQ3}),1.0]])]});}
            var Q19;
            {var subQ0=sQuery(id+"F0.wireOp",EDGE,"E7");var subQ1=sQuery(id+"F0.wireOp",EDGE,"E3");var subQ2=makeQuery(id+"F0.imprint","INTERSECT",VERTEX,{"derivedFrom":[subQ1,subQ0]});Q19=makeQuery(id+"F0.imprint","IMPRINT",FACE,{"disambiguationData":[TD([[makeQuery(id+"F0.imprint","IMPRINT",EDGE,{"disambiguationData":[TD([[subQ2,-1.0]])],"derivedFrom":subQ1}),-1.0]])]});}
            var Q20;
            {var subQ0=sQuery(id+"F0.wireOp",EDGE,"E3");var subQ3=sQuery(id+"F0.wireOp",EDGE,"E7");var subQ5=makeQuery(id+"F0.imprint","INTERSECT",VERTEX,{"derivedFrom":[subQ0,subQ3]});Q20=makeQuery(id+"F0.imprint","IMPRINT",FACE,{"disambiguationData":[TD([[makeQuery(id+"F0.imprint","IMPRINT",EDGE,{"disambiguationData":[TD([[subQ5,-1.0]])],"derivedFrom":subQ3}),1.0]])]});}
            var Q21;
            {var subQ0=sQuery(id+"F0.wireOp",EDGE,"E5");var subQ1=sQuery(id+"F0.wireOp",EDGE,"E2");var subQ2=makeQuery(id+"F0.imprint","INTERSECT",VERTEX,{"derivedFrom":[subQ1,subQ0]});Q21=makeQuery(id+"F0.imprint","IMPRINT",FACE,{"disambiguationData":[TD([[makeQuery(id+"F0.imprint","IMPRINT",EDGE,{"disambiguationData":[TD([[subQ2,-1.0]])],"derivedFrom":subQ1}),-1.0]])]});}
            var Q22;
            {var subQ0=sQuery(id+"F0.wireOp",EDGE,"E5");var subQ1=sQuery(id+"F0.wireOp",EDGE,"E2");var subQ2=makeQuery(id+"F0.imprint","INTERSECT",VERTEX,{"derivedFrom":[subQ1,subQ0]});Q22=makeQuery(id+"F0.imprint","IMPRINT",FACE,{"disambiguationData":[TD([[makeQuery(id+"F0.imprint","IMPRINT",EDGE,{"disambiguationData":[TD([[subQ2,-1.0]])],"derivedFrom":subQ1}),1.0]])]});}
            var Q23;
            {var subQ0=sQuery(id+"F0.wireOp",EDGE,"E8");var subQ1=sQuery(id+"F0.wireOp",EDGE,"E4");var subQ2=makeQuery(id+"F0.imprint","INTERSECT",VERTEX,{"derivedFrom":[subQ1,subQ0]});Q23=makeQuery(id+"F0.imprint","IMPRINT",FACE,{"disambiguationData":[TD([[makeQuery(id+"F0.imprint","IMPRINT",EDGE,{"disambiguationData":[TD([[subQ2,-1.0]])],"derivedFrom":subQ1}),1.0]])]});}
            var Q24;
            {var subQ0=sQuery(id+"F0.wireOp",EDGE,"E6");var subQ1=sQuery(id+"F0.wireOp",EDGE,"E4");var subQ2=makeQuery(id+"F0.imprint","INTERSECT",VERTEX,{"derivedFrom":[subQ1,subQ0]});Q24=makeQuery(id+"F0.imprint","IMPRINT",FACE,{"disambiguationData":[TD([[makeQuery(id+"F0.imprint","IMPRINT",EDGE,{"disambiguationData":[TD([[subQ2,-1.0]])],"derivedFrom":subQ1}),1.0]])]});}
            var Q25;
            {var subQ0=sQuery(id+"F0.wireOp",EDGE,"E8");var subQ1=sQuery(id+"F0.wireOp",EDGE,"E3");var subQ2=makeQuery(id+"F0.imprint","INTERSECT",VERTEX,{"derivedFrom":[subQ1,subQ0]});Q25=makeQuery(id+"F0.imprint","IMPRINT",FACE,{"disambiguationData":[TD([[makeQuery(id+"F0.imprint","IMPRINT",EDGE,{"disambiguationData":[TD([[subQ2,-1.0]])],"derivedFrom":subQ1}),1.0]])]});}
            var Q26;
            {var subQ0=sQuery(id+"F0.wireOp",EDGE,"E7");var subQ1=sQuery(id+"F0.wireOp",EDGE,"E3");var subQ2=makeQuery(id+"F0.imprint","INTERSECT",VERTEX,{"derivedFrom":[subQ1,subQ0]});Q26=makeQuery(id+"F0.imprint","IMPRINT",FACE,{"disambiguationData":[TD([[makeQuery(id+"F0.imprint","IMPRINT",EDGE,{"disambiguationData":[TD([[subQ2,-1.0]])],"derivedFrom":subQ1}),1.0]])]});}
            var Q27;
            {var subQ0=sQuery(id+"F0.wireOp",EDGE,"E8");var subQ1=sQuery(id+"F0.wireOp",EDGE,"E2");var subQ2=makeQuery(id+"F0.imprint","INTERSECT",VERTEX,{"derivedFrom":[subQ1,subQ0]});Q27=makeQuery(id+"F0.imprint","IMPRINT",FACE,{"disambiguationData":[TD([[makeQuery(id+"F0.imprint","IMPRINT",EDGE,{"disambiguationData":[TD([[subQ2,-1.0]])],"derivedFrom":subQ1}),1.0]])]});}
            var Q28;
            {var subQ0=sQuery(id+"F0.wireOp",EDGE,"E8");var subQ5=makeQuery(id+"F0.imprint","INTERSECT",VERTEX,{"derivedFrom":[sQuery(id+"F0.wireOp",EDGE,"E4"),subQ0]});Q28=makeQuery(id+"F0.imprint","IMPRINT",FACE,{"disambiguationData":[TD([[makeQuery(id+"F0.imprint","IMPRINT",EDGE,{"disambiguationData":[TD([[subQ5,-1.0]])],"derivedFrom":subQ0}),1.0]])]});}
            extrude(context, id + "F6", {"entities" : qUnion([Q0, Q1, Q2, Q3, Q4, Q5, Q6, Q7, Q8, Q9, Q10, Q11, Q12, Q13, Q14, Q15, Q16, Q17, Q18, Q19, Q20, Q21, Q22, Q23, Q24, Q25, Q26, Q27, Q28]), "depth" : 2.5 * mm});
        }
    });
